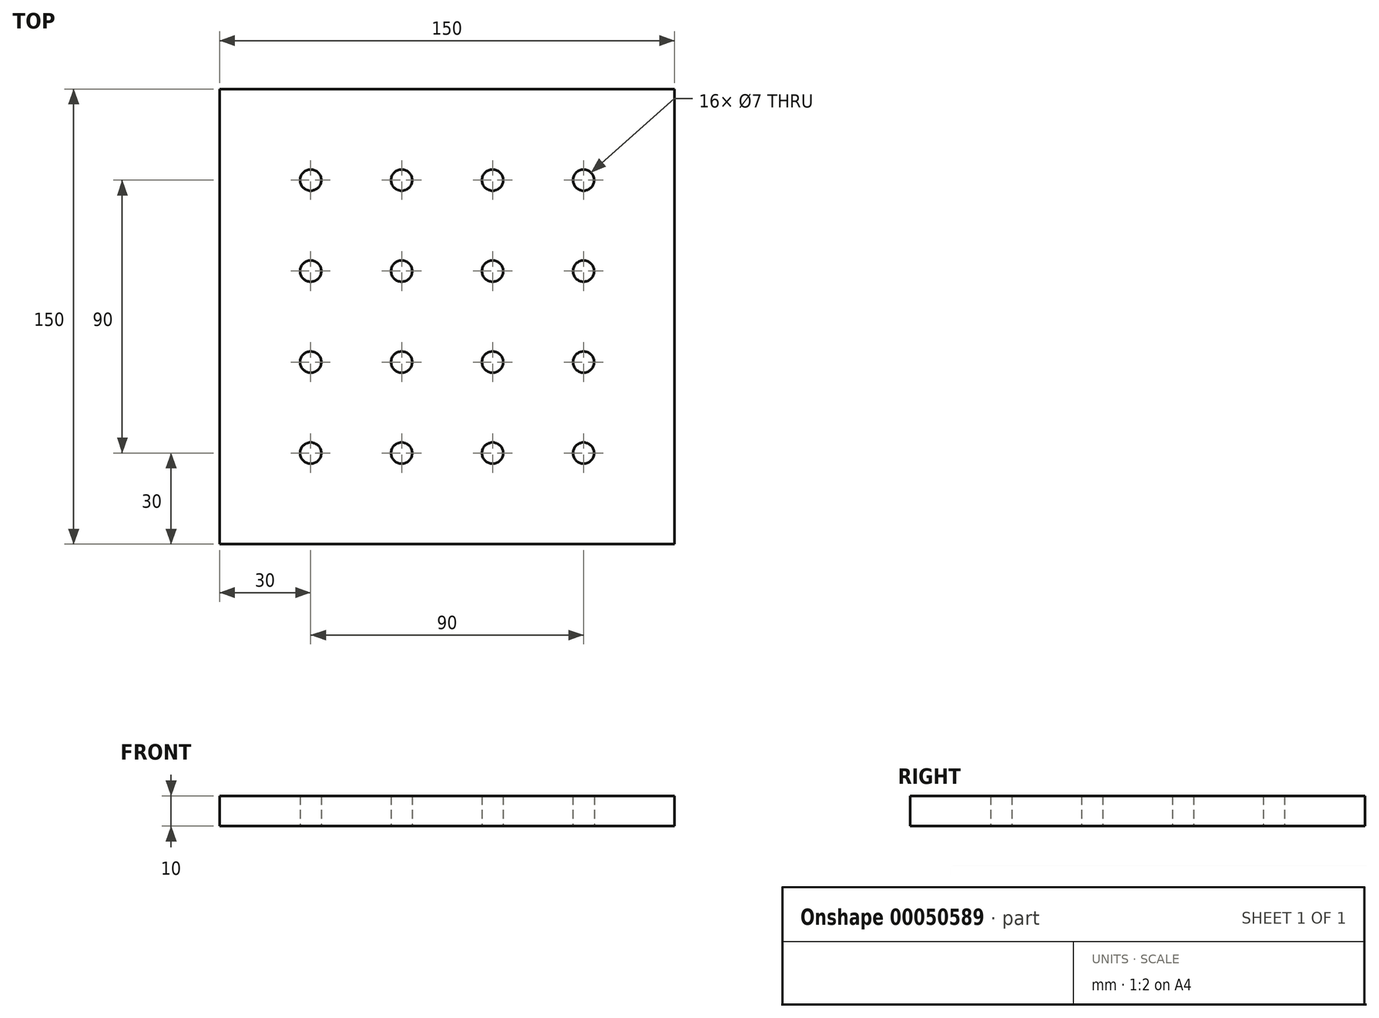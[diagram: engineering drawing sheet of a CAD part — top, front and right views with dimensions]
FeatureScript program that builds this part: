
annotation { "Feature Type Name" : "Feature", "Feature Type Description" : "" }
export const myFeature = defineFeature(function(context is Context, id is Id, definition is map)
    precondition{}
    {
        {
            var Q0;
            Q0=qCreatedBy(makeId("Top.planeOp"),FACE);
            var sketch = newSketch(context, id + "F0", { "sketchPlane" : qUnion([Q0])});
            skLineSegment(sketch, "E0.bottom", {"start": v(0, 0) * mm, "end": v(-150, 0) * mm});
            skLineSegment(sketch, "E0.top", {"start": v(0, -150) * mm, "end": v(-150, -150) * mm});
            skLineSegment(sketch, "E0.left", {"start": v(0, 0) * mm, "end": v(0, -150) * mm});
            skLineSegment(sketch, "E0.right", {"start": v(-150, 0) * mm, "end": v(-150, -150) * mm});
            skCircle(sketch, "E1", {"center": v(-120, -120) * mm, "radius": 3.5 * mm});
            skCircle(sketch, "E2.0.1.0", {"center": v(-120, -90) * mm, "radius": 3.5 * mm});
            skCircle(sketch, "E2.0.2.0", {"center": v(-120, -60) * mm, "radius": 3.5 * mm});
            skCircle(sketch, "E2.0.3.0", {"center": v(-120, -30) * mm, "radius": 3.5 * mm});
            skCircle(sketch, "E2.1.0.0", {"center": v(-90, -120) * mm, "radius": 3.5 * mm});
            skCircle(sketch, "E2.1.1.0", {"center": v(-90, -90) * mm, "radius": 3.5 * mm});
            skCircle(sketch, "E2.1.2.0", {"center": v(-90, -60) * mm, "radius": 3.5 * mm});
            skCircle(sketch, "E2.1.3.0", {"center": v(-90, -30) * mm, "radius": 3.5 * mm});
            skCircle(sketch, "E2.2.0.0", {"center": v(-60, -120) * mm, "radius": 3.5 * mm});
            skCircle(sketch, "E2.2.1.0", {"center": v(-60, -90) * mm, "radius": 3.5 * mm});
            skCircle(sketch, "E2.2.2.0", {"center": v(-60, -60) * mm, "radius": 3.5 * mm});
            skCircle(sketch, "E2.2.3.0", {"center": v(-60, -30) * mm, "radius": 3.5 * mm});
            skCircle(sketch, "E2.3.0.0", {"center": v(-30, -120) * mm, "radius": 3.5 * mm});
            skCircle(sketch, "E2.3.1.0", {"center": v(-30, -90) * mm, "radius": 3.5 * mm});
            skCircle(sketch, "E2.3.2.0", {"center": v(-30, -60) * mm, "radius": 3.5 * mm});
            skCircle(sketch, "E2.3.3.0", {"center": v(-30, -30) * mm, "radius": 3.5 * mm});
            skLineSegment(sketch, "E2.direction1", {"start": v(-120, -120) * mm, "end": v(-90, -120) * mm, "construction": true});
            skLineSegment(sketch, "E2.direction2", {"start": v(-120, -120) * mm, "end": v(-120, -90) * mm, "construction": true});
            skSolve(sketch);
        }
        {
            var Q0;
            Q0=makeQuery(id+"F0.imprint","IMPRINT",FACE,{"disambiguationData":[TD([[makeQuery(id+"F0.imprint","IMPRINT",EDGE,{"derivedFrom":sQuery(id+"F0.wireOp",EDGE,"E0.bottom")}),1.0]])]});
            extrude(context, id + "F1", {"entities" : qUnion([Q0]), "depth" : 10 * mm});
        }
    });
